# Revit family: AL120
name_source: partatom
category: Двери
revit_build: Autodesk Revit 2016 (Build: 20160314_0715(x64)
units: mm (PartAtom-declared; Revit-internal decimal feet)

## family parameters
Всегда вертикально = Да
Заголовок OmniClass = Doors
Номер OmniClass = 23.30.10.00
Общий = Нет
Основа = Стена
При загрузке вырезать с полостями = Нет
Точка расчета площади = Нет

## types (2) — shared parameters
ADSK_URL страницы изделия = https://www.fire-tec.ru
ADSK_Завод-изготовитель = Firetechnics
ADSK_Наименование = Рулонные противопожарные ворота FireTechnics-S EI60 с миниральным заполнителем
ADSK_Предел огнестойкости = EI120
ADSK_Размер_Высота = 3000 мм
ADSK_Размер_Ширина = 3000 мм
BL_ВысотаКороба = 297 мм
BL_ДлинаНаправляющей = 60 мм
BL_КоличествоФаз = 1
BL_МатериалНаправляющих = BL_Сталь_Оцинкованная_Листовая_2мм_Firetechnics
BL_МатериалПолотна = BL_АлюминийсДвойнойСтенкой_ВнутреннимНаполнениемизЖесткогоППУ_ПорошковойПокраскойпоRALs_Firetechnics
BL_Напряжение = 220 В
BL_ОтстаяниеотДвигателя = 130 мм
BL_ШиринаBходавПолотна = 40 мм
BL_ШиринаВерхнейНаправляющей = 374 мм
BL_ШиринаНаправляющих = 115 мм
BL_ШиринаПолотна = 75 мм
URL = https://www.fire-tec.ru
Аналитическая конструкция = <Нет>
Высота = 3000 мм
Замыкание стены = По основе
Изготовитель = Firetechnics
Огнестойкость = AL120
Функция = Внутренние слои
Ширина = 3000 мм
Штора открыто/закрыто = Да
zero-valued in all types: BL_РазмерШага

## type names (no varying parameters)
- AL-120
- AL120

## geometry (parser evidence)
native form markers: Blend x2
no freeform markers — native parametric forms only
